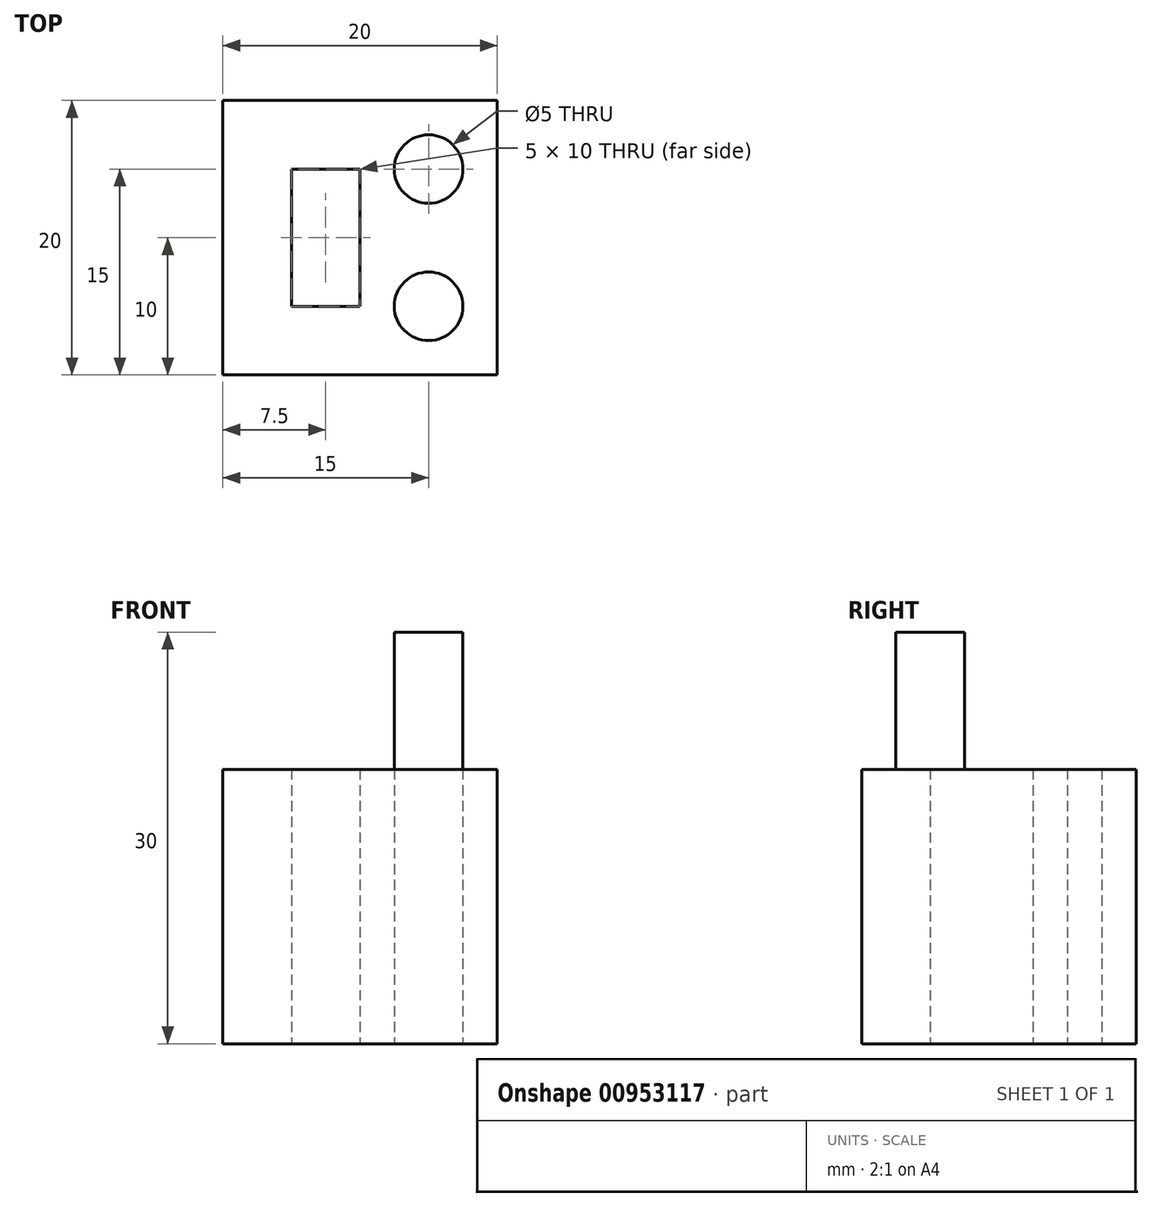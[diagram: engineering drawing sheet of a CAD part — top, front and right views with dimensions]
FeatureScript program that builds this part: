
annotation { "Feature Type Name" : "Feature", "Feature Type Description" : "" }
export const myFeature = defineFeature(function(context is Context, id is Id, definition is map)
    precondition{}
    {
        {
            var Q0;
            Q0=qCreatedBy(makeId("Top.planeOp"),FACE);
            var sketch = newSketch(context, id + "F0", { "sketchPlane" : qUnion([Q0])});
            skLineSegment(sketch, "E0.bottom", {"start": v(10, -10) * mm, "end": v(-10, -10) * mm});
            skLineSegment(sketch, "E0.top", {"start": v(10, 10) * mm, "end": v(-10, 10) * mm});
            skLineSegment(sketch, "E0.left", {"start": v(10, -10) * mm, "end": v(10, 10) * mm});
            skLineSegment(sketch, "E0.right", {"start": v(-10, -10) * mm, "end": v(-10, 10) * mm});
            skPoint(sketch, "E0.middle", {"position": v(0, 0) * mm});
            skLineSegment(sketch, "E1.bottom", {"start": v(-5, 5) * mm, "end": v(0, 5) * mm});
            skLineSegment(sketch, "E1.top", {"start": v(-5, -5) * mm, "end": v(0, -5) * mm});
            skLineSegment(sketch, "E1.left", {"start": v(-5, 5) * mm, "end": v(-5, -5) * mm});
            skLineSegment(sketch, "E1.right", {"start": v(0, 5) * mm, "end": v(0, -5) * mm});
            skCircle(sketch, "E2", {"center": v(5, 5) * mm, "radius": 2.5 * mm});
            skSolve(sketch);
        }
        {
            var Q0;
            Q0=makeQuery(id+"F0.imprint","IMPRINT",FACE,{"disambiguationData":[TD([[makeQuery(id+"F0.imprint","IMPRINT",EDGE,{"derivedFrom":sQuery(id+"F0.wireOp",EDGE,"E0.bottom")}),-1.0]])]});
            extrude(context, id + "F1", {"entities" : qUnion([Q0]), "depth" : 20 * mm, "offsetDistance" : 25 * mm});
        }
        {
            var Q0;
            Q0=makeQuery(id+"F1.opExtrude","CAP_FACE",FACE,{"disambiguationData":[OSD([sQuery(id+"F0.wireOp",EDGE,"E0.bottom"),sQuery(id+"F0.wireOp",EDGE,"E0.top"),sQuery(id+"F0.wireOp",EDGE,"E0.left"),sQuery(id+"F0.wireOp",EDGE,"E0.right"),sQuery(id+"F0.wireOp",EDGE,"E1.bottom"),sQuery(id+"F0.wireOp",EDGE,"E1.top"),sQuery(id+"F0.wireOp",EDGE,"E1.left"),sQuery(id+"F0.wireOp",EDGE,"E1.right"),sQuery(id+"F0.wireOp",EDGE,"E2")])],"isStart":false});
            var sketch = newSketch(context, id + "F2", { "sketchPlane" : qUnion([Q0])});
            skCircle(sketch, "E3", {"center": v(5, -5) * mm, "radius": 2.5 * mm});
            skSolve(sketch);
        }
        {
            var Q0;
            Q0=makeQuery(id+"F2.imprint","IMPRINT",FACE,{"disambiguationData":[TD([[makeQuery(id+"F2.imprint","IMPRINT",EDGE,{"derivedFrom":sQuery(id+"F2.wireOp",EDGE,"E3")}),1.0]])]});
            extrude(context, id + "F3", {"entities" : qUnion([Q0]), "operationType" : NewBodyOperationType.ADD, "depth" : 10 * mm, "offsetDistance" : 25 * mm});
        }
    });
